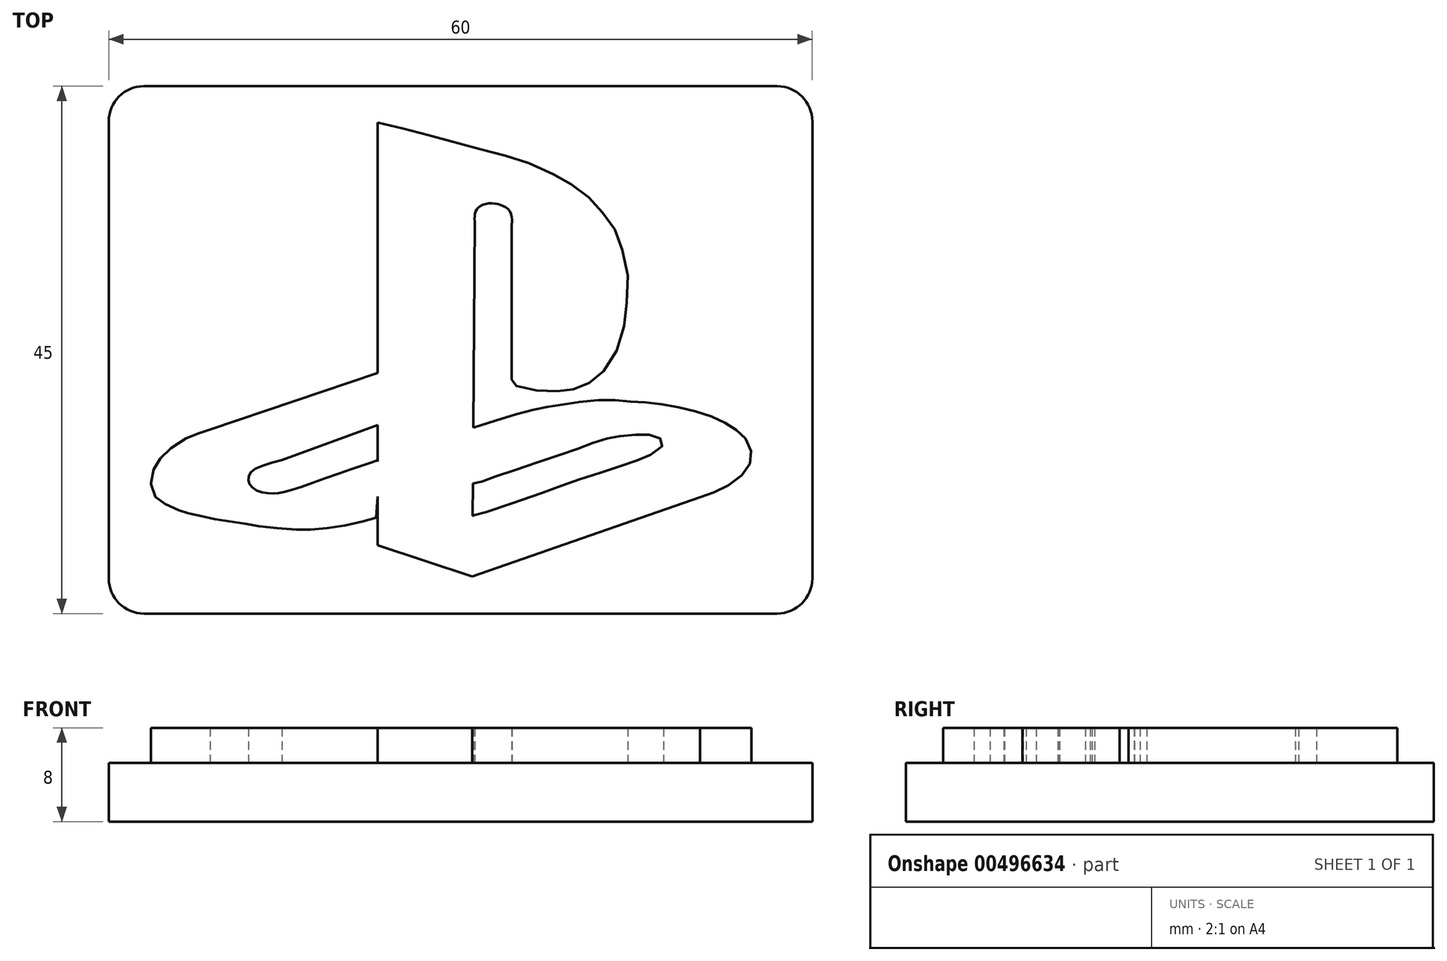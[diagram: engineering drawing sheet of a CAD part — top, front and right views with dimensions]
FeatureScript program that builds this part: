
annotation { "Feature Type Name" : "Feature", "Feature Type Description" : "" }
export const myFeature = defineFeature(function(context is Context, id is Id, definition is map)
    precondition{}
    {
        {
            var Q0;
            Q0=qCreatedBy(makeId("Top.planeOp"),FACE);
            var sketch = newSketch(context, id + "F0", { "sketchPlane" : qUnion([Q0])});
            skLineSegment(sketch, "E0", {"start": v(-6.6, -3.1) * mm, "end": v(-6.6, -39.19) * mm});
            skLineSegment(sketch, "E1", {"start": v(-6.6, -39.19) * mm, "end": v(1.48, -41.82) * mm});
            skLineSegment(sketch, "E2", {"start": v(1.48, -41.82) * mm, "end": v(1.69, -11.52) * mm});
            skFitSpline(sketch, "E3", {"points": [v(1.69, -11.52) * mm, v(1.69, -11.05) * mm, v(1.8, -10.6) * mm, v(2.11, -10.26) * mm, v(2.77, -10.01) * mm, v(3.56, -10.03) * mm, v(4.07, -10.22) * mm, v(4.64, -10.61) * mm, v(4.85, -11.28) * mm, v(4.85, -11.8) * mm], "startDerivative": vector(-0.23, 4.72) * mm, "endDerivative": vector(-0.2, -4.7) * mm});
            skLineSegment(sketch, "E4", {"start": v(4.85, -11.8) * mm, "end": v(4.85, -16.25) * mm});
            skLineSegment(sketch, "E5", {"start": v(4.85, -16.25) * mm, "end": v(4.85, -25.04) * mm});
            skFitSpline(sketch, "E6", {"points": [v(4.85, -25.04) * mm, v(4.85, -25.5) * mm, v(4.98, -25.52) * mm, v(6.3, -25.86) * mm, v(7.84, -26.02) * mm, v(9.4, -25.99) * mm, v(10.13, -25.85) * mm, v(11.17, -25.47) * mm, v(12.22, -24.76) * mm, v(13.4, -23.35) * mm, v(14.35, -20.9) * mm, v(14.63, -18.84) * mm, v(14.71, -16) * mm, v(14.13, -13.57) * mm, v(13.51, -11.97) * mm, v(12.46, -10.63) * mm, v(11.37, -9.45) * mm, v(9.89, -8.35) * mm, v(8.5, -7.57) * mm, v(6.02, -6.47) * mm, v(3.82, -5.81) * mm, v(1.29, -5.14) * mm, v(-1.4, -4.41) * mm, v(-4.07, -3.7) * mm, v(-6.6, -3.1) * mm], "startDerivative": vector(-2.71, -28.4) * mm, "endDerivative": vector(-47.93, 11.91) * mm});
            skLineSegment(sketch, "E7", {"start": v(1.48, -41.82) * mm, "end": v(20.9, -35.06) * mm});
            skFitSpline(sketch, "E8", {"points": [v(20.9, -35.06) * mm, v(22.73, -34.37) * mm, v(24.7, -32.93) * mm, v(25.28, -31.57) * mm, v(24.78, -30.05) * mm, v(23.66, -29.11) * mm, v(22.15, -28.29) * mm, v(19.63, -27.51) * mm, v(17.1, -27.07) * mm, v(15.05, -26.9) * mm, v(12.82, -26.78) * mm, v(9.9, -27.04) * mm, v(7.82, -27.4) * mm, v(5.66, -27.88) * mm, v(1.57, -29.13) * mm], "startDerivative": vector(26.65, 8.24) * mm, "endDerivative": vector(-44.5, -14.33) * mm});
            skFitSpline(sketch, "E9", {"points": [v(1.53, -33.9) * mm, v(2.02, -33.84) * mm, v(3.04, -33.47) * mm, v(5.8, -32.52) * mm, v(9.34, -31.33) * mm, v(11.25, -30.64) * mm, v(12.86, -30.08) * mm, v(13.9, -29.89) * mm, v(15.6, -29.73) * mm, v(16.74, -29.8) * mm, v(17.6, -30.14) * mm, v(17.76, -30.56) * mm, v(16.83, -31.39) * mm, v(15.46, -31.94) * mm, v(13.25, -32.72) * mm, v(10.1, -33.73) * mm, v(7.57, -34.65) * mm, v(2.33, -36.43) * mm, v(1.68, -36.6) * mm, v(1.51, -36.66) * mm], "startDerivative": vector(15.72, 0.87) * mm, "endDerivative": vector(-8.7, -3.61) * mm});
            skLineSegment(sketch, "E10", {"start": v(-6.6, -24.46) * mm, "end": v(-20.88, -29.3) * mm});
            skFitSpline(sketch, "E11", {"points": [v(-20.88, -29.3) * mm, v(-21.8, -29.62) * mm, v(-22.17, -29.72) * mm, v(-23.31, -30.26) * mm, v(-24.52, -31.14) * mm, v(-25.25, -31.92) * mm, v(-25.67, -32.65) * mm, v(-25.9, -33.53) * mm, v(-25.78, -34.7) * mm, v(-25.35, -35.23) * mm, v(-24.68, -35.68) * mm, v(-23.62, -36.15) * mm, v(-23.08, -36.34) * mm, v(-22.6, -36.47) * mm, v(-21.58, -36.7) * mm, v(-20.78, -36.88) * mm, v(-19.51, -37.08) * mm, v(-18.73, -37.2) * mm, v(-17.34, -37.42) * mm, v(-16.43, -37.58) * mm, v(-14.5, -37.77) * mm, v(-12.96, -37.84) * mm, v(-12.09, -37.81) * mm, v(-10.58, -37.67) * mm, v(-8.94, -37.39) * mm, v(-7.41, -37.03) * mm, v(-6.7, -36.81) * mm, v(-6.67, -36.74) * mm, v(-6.61, -31.97) * mm, v(-6.72, -31.95) * mm, v(-10.4, -33.23) * mm, v(-14.63, -34.66) * mm, v(-15.6, -34.76) * mm, v(-16.8, -34.55) * mm, v(-17.46, -34.04) * mm, v(-17.62, -33.47) * mm, v(-17.33, -32.85) * mm, v(-14.75, -31.89) * mm], "startDerivative": vector(-41.64, -15.79) * mm, "endDerivative": vector(76.58, 20.42) * mm});
            skLineSegment(sketch, "E12", {"start": v(-14.75, -31.89) * mm, "end": v(-6.6, -28.9) * mm});
            skLineSegment(sketch, "E13", {"start": v(-6.6, -28.9) * mm, "end": v(-6.72, -31.95) * mm});
            skLineSegment(sketch, "E14", {"start": v(1.68, -33.9) * mm, "end": v(1.68, -36.6) * mm});
            skLineSegment(sketch, "E15", {"start": v(-6.6, -28.9) * mm, "end": v(-6.63, -24.47) * mm});
            skSolve(sketch);
        }
        {
            var Q0;
            Q0=qCreatedBy(makeId("Top.planeOp"),FACE);
            var sketch = newSketch(context, id + "F1", { "sketchPlane" : qUnion([Q0])});
            skLineSegment(sketch, "E16.bottom", {"start": v(-26.53, 0) * mm, "end": v(27.47, 0) * mm});
            skLineSegment(sketch, "E16.top", {"start": v(-26.53, -45) * mm, "end": v(27.47, -45) * mm});
            skLineSegment(sketch, "E16.left", {"start": v(-29.53, -3) * mm, "end": v(-29.53, -42) * mm});
            skLineSegment(sketch, "E16.right", {"start": v(30.47, -3) * mm, "end": v(30.47, -42) * mm});
            skPoint(sketch, "E17.visualSharp", {"position": v(-29.53, 0) * mm});
            skArc(sketch, "E17.filletArc", {"start": v(-26.53, 0) * mm, "mid": v(-28.65, -0.88) * mm, "end": v(-29.53, -3) * mm});
            skPoint(sketch, "E18.visualSharp", {"position": v(30.47, 0) * mm});
            skArc(sketch, "E18.filletArc", {"start": v(30.47, -3) * mm, "mid": v(29.6, -0.88) * mm, "end": v(27.47, 0) * mm});
            skPoint(sketch, "E19.visualSharp", {"position": v(30.47, -45) * mm});
            skArc(sketch, "E19.filletArc", {"start": v(27.47, -45) * mm, "mid": v(29.6, -44.12) * mm, "end": v(30.47, -42) * mm});
            skPoint(sketch, "E20.visualSharp", {"position": v(-29.53, -45) * mm});
            skArc(sketch, "E20.filletArc", {"start": v(-29.53, -42) * mm, "mid": v(-28.65, -44.12) * mm, "end": v(-26.53, -45) * mm});
            skSolve(sketch);
        }
        {
            var Q0;
            Q0 = qSketchRegion(id + "F1", true);
            extrude(context, id + "F2", {"entities" : qUnion([Q0]), "depth" : 5 * mm, "offsetDistance" : 25 * mm});
        }
        {
            var Q0;
            Q0 = qSketchRegion(id + "F0", true);
            extrude(context, id + "F3", {"entities" : qUnion([Q0]), "operationType" : NewBodyOperationType.ADD, "depth" : 8 * mm, "offsetDistance" : 25 * mm});
        }
    });
